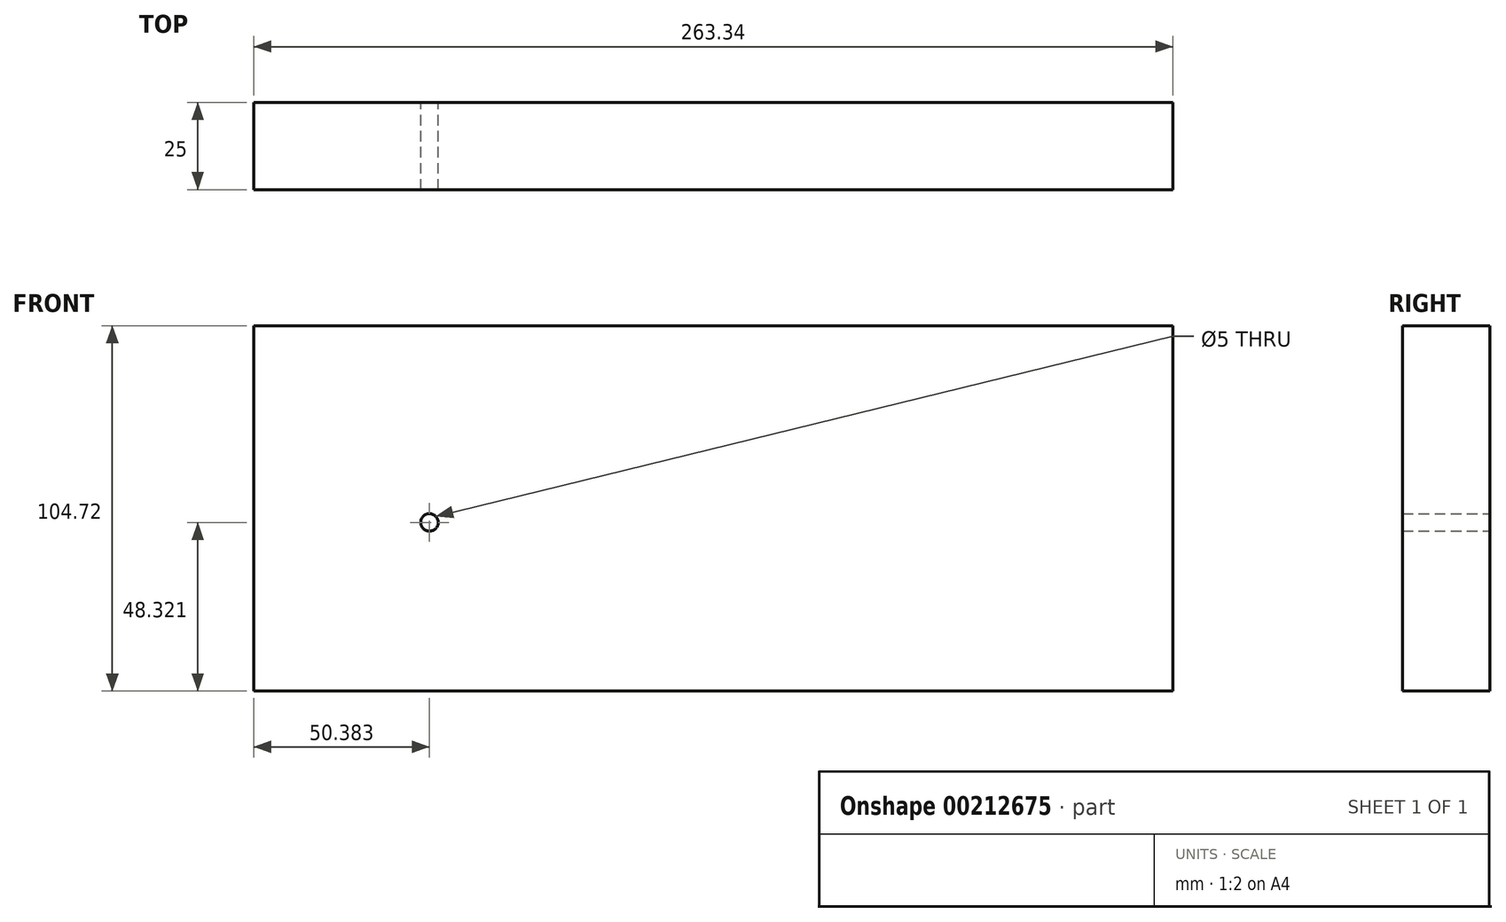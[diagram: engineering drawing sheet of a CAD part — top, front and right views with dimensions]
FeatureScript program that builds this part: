
annotation { "Feature Type Name" : "Feature", "Feature Type Description" : "" }
export const myFeature = defineFeature(function(context is Context, id is Id, definition is map)
    precondition{}
    {
        {
            var Q0;
            Q0=qCreatedBy(makeId("Front.planeOp"),FACE);
            var sketch = newSketch(context, id + "F0", { "sketchPlane" : qUnion([Q0])});
            skLineSegment(sketch, "E0.bottom", {"start": v(-115.76, 38.66) * mm, "end": v(147.58, 38.66) * mm});
            skLineSegment(sketch, "E0.top", {"start": v(-115.76, -66.06) * mm, "end": v(147.58, -66.06) * mm});
            skLineSegment(sketch, "E0.left", {"start": v(-115.76, 38.66) * mm, "end": v(-115.76, -66.06) * mm});
            skLineSegment(sketch, "E0.right", {"start": v(147.58, 38.66) * mm, "end": v(147.58, -66.06) * mm});
            skPoint(sketch, "E1", {"position": v(-65.38, -17.74) * mm});
            skSolve(sketch);
        }
        {
            var Q0;
            Q0=makeQuery(id+"F0.imprint","IMPRINT",FACE,{"disambiguationData":[TD([[makeQuery(id+"F0.imprint","IMPRINT",EDGE,{"derivedFrom":sQuery(id+"F0.wireOp",EDGE,"E0.bottom")}),-1.0]])]});
            extrude(context, id + "F1", {"entities" : qUnion([Q0]), "depth" : 25 * mm});
        }
        {
            var Q0;
            Q0=sQuery(id+"F0.wireOp",VERTEX,"E1");
            var Q1;
            Q1=makeQuery(id+"F1.opExtrude","SWEPT_BODY",BODY,{"disambiguationData":[OSD([sQuery(id+"F0.wireOp",EDGE,"E0.bottom"),sQuery(id+"F0.wireOp",EDGE,"E0.top"),sQuery(id+"F0.wireOp",EDGE,"E0.left"),sQuery(id+"F0.wireOp",EDGE,"E0.right")])]});
            hole(context, id + "F2", {"style" : HoleStyle.SIMPLE, "endStyle" : HoleEndStyle.THROUGH, "oppositeDirection" : true, "holeDiameter" : 5 * mm, "locations" : qUnion([Q0]), "scope" : qUnion([Q1]), "isTappedThrough" : true});
        }
    });
